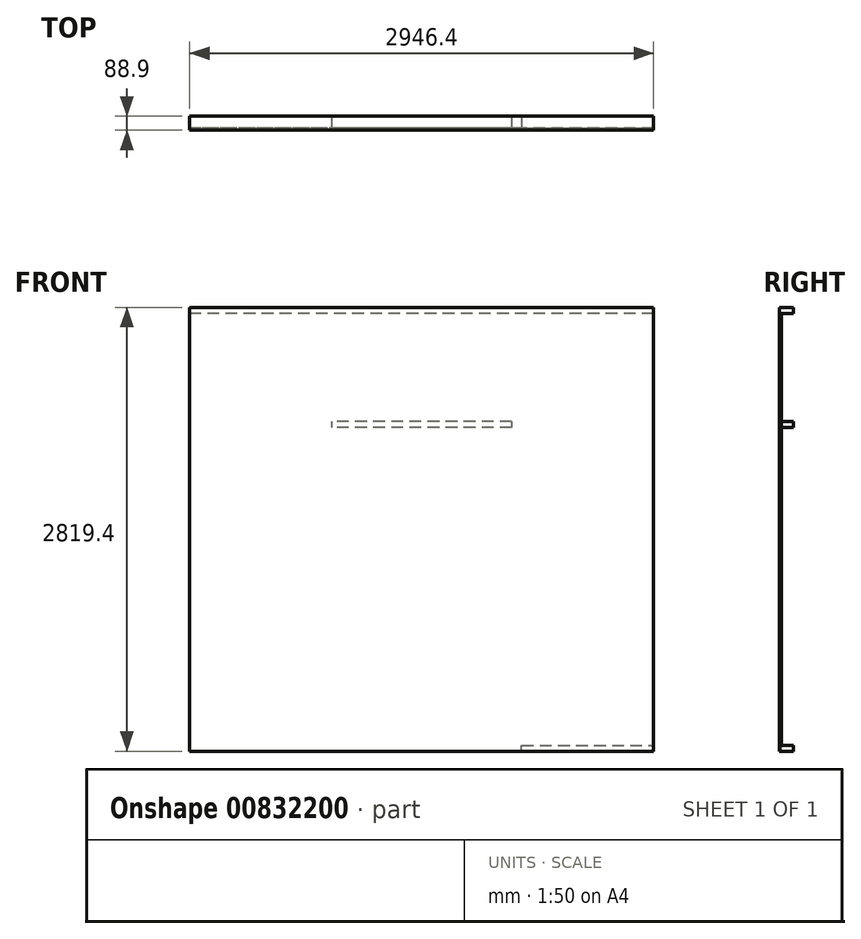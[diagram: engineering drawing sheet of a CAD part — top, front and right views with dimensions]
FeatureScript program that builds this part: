
annotation { "Feature Type Name" : "Feature", "Feature Type Description" : "" }
export const myFeature = defineFeature(function(context is Context, id is Id, definition is map)
    precondition{}
    {
        {
            var Q0;
            Q0=qCreatedBy(makeId("Front.planeOp"),FACE);
            var sketch = newSketch(context, id + "F0", { "sketchPlane" : qUnion([Q0])});
            skLineSegment(sketch, "E0.bottom", {"start": v(1473.2, 1409.7) * mm, "end": v(-1473.2, 1409.7) * mm});
            skLineSegment(sketch, "E0.left", {"start": v(1473.2, 1409.7) * mm, "end": v(1473.2, -1409.7) * mm});
            skLineSegment(sketch, "E0.right", {"start": v(-1473.2, 1409.7) * mm, "end": v(-1473.2, -1409.7) * mm});
            skLineSegment(sketch, "E1.trimOffspring", {"start": v(1473.2, -1409.7) * mm, "end": v(-1473.2, -1409.7) * mm});
            skSolve(sketch);
        }
        {
            var Q0;
            Q0=qSketchRegion(id+"F0",true);
            extrude(context, id + "F1", {"entities" : qUnion([Q0]), "depth" : 12.7 * mm, "offsetDistance" : 25.4 * mm});
        }
        {
            var Q0;
            Q0=makeQuery(id+"F1.opExtrude","CAP_FACE",FACE,{"disambiguationData":[OSD([sQuery(id+"F0.wireOp",EDGE,"E0.bottom"),sQuery(id+"F0.wireOp",EDGE,"E0.top"),sQuery(id+"F0.wireOp",EDGE,"E0.left"),sQuery(id+"F0.wireOp",EDGE,"E0.right"),sQuery(id+"F0.wireOp",EDGE,"iS1P1Vp1-wRpF-BQkS-J5lC-1q9Rx3VtRRPI.top"),sQuery(id+"F0.wireOp",EDGE,"iS1P1Vp1-wRpF-BQkS-J5lC-1q9Rx3VtRRPI.left"),sQuery(id+"F0.wireOp",EDGE,"iS1P1Vp1-wRpF-BQkS-J5lC-1q9Rx3VtRRPI.right"),sQuery(id+"F0.wireOp",EDGE,"E1.trimOffspring")])],"isStart":true});
            var sketch = newSketch(context, id + "F2", { "sketchPlane" : qUnion([Q0])});
            skLineSegment(sketch, "E2.bottom", {"start": v(-1473.2, 1409.7) * mm, "end": v(1473.2, 1409.7) * mm});
            skLineSegment(sketch, "E2.top", {"start": v(-1473.2, 1371.6) * mm, "end": v(1473.2, 1371.6) * mm});
            skLineSegment(sketch, "E2.left", {"start": v(-1473.2, 1409.7) * mm, "end": v(-1473.2, 1371.6) * mm});
            skLineSegment(sketch, "E2.right", {"start": v(1473.2, 1409.7) * mm, "end": v(1473.2, 1371.6) * mm});
            skLineSegment(sketch, "E3.bottom", {"start": v(1473.2, 1371.6) * mm, "end": v(1435.1, 1371.6) * mm});
            skLineSegment(sketch, "E3.top", {"start": v(1473.2, -1371.6) * mm, "end": v(1435.1, -1371.6) * mm});
            skLineSegment(sketch, "E3.left", {"start": v(1473.2, 1371.6) * mm, "end": v(1473.2, -1371.6) * mm});
            skLineSegment(sketch, "E3.right", {"start": v(1435.1, 1371.6) * mm, "end": v(1435.1, -1371.6) * mm});
            skLineSegment(sketch, "E4.bottom", {"start": v(1473.2, -1371.6) * mm, "end": v(-1473.2, -1371.6) * mm});
            skLineSegment(sketch, "E4.top", {"start": v(1473.2, -1409.7) * mm, "end": v(-1473.2, -1409.7) * mm});
            skLineSegment(sketch, "E4.left", {"start": v(1473.2, -1371.6) * mm, "end": v(1473.2, -1409.7) * mm});
            skLineSegment(sketch, "E4.right", {"start": v(-1473.2, -1371.6) * mm, "end": v(-1473.2, -1409.7) * mm});
            skLineSegment(sketch, "E5.bottom", {"start": v(-1473.2, -1371.6) * mm, "end": v(-1435.1, -1371.6) * mm});
            skLineSegment(sketch, "E5.top", {"start": v(-1473.2, 1371.6) * mm, "end": v(-1435.1, 1371.6) * mm});
            skLineSegment(sketch, "E5.left", {"start": v(-1473.2, -1371.6) * mm, "end": v(-1473.2, 1371.6) * mm});
            skLineSegment(sketch, "E5.right", {"start": v(-1435.1, -1371.6) * mm, "end": v(-1435.1, 1371.6) * mm});
            skLineSegment(sketch, "E6.left", {"start": v(-1473.2, 762) * mm, "end": v(-1473.2, 723.9) * mm});
            skLineSegment(sketch, "E7.bottom", {"start": v(-635, -1409.7) * mm, "end": v(-1473.2, -1409.7) * mm});
            skLineSegment(sketch, "E7.top", {"start": v(-635, -1371.6) * mm, "end": v(-1473.2, -1371.6) * mm});
            skLineSegment(sketch, "E7.left", {"start": v(-635, -1409.7) * mm, "end": v(-635, -1371.6) * mm});
            skLineSegment(sketch, "E7.right", {"start": v(-1473.2, -1409.7) * mm, "end": v(-1473.2, -1371.6) * mm});
            skLineSegment(sketch, "E8.bottom", {"start": v(-1079.5, 1371.6) * mm, "end": v(-1041.4, 1371.6) * mm});
            skLineSegment(sketch, "E8.top", {"start": v(-1079.5, -1371.6) * mm, "end": v(-1041.4, -1371.6) * mm});
            skLineSegment(sketch, "E8.left", {"start": v(-1079.5, 1371.6) * mm, "end": v(-1079.5, -1371.6) * mm});
            skLineSegment(sketch, "E8.right", {"start": v(-1041.4, 1371.6) * mm, "end": v(-1041.4, -1371.6) * mm});
            skLineSegment(sketch, "E9.bottom", {"start": v(-635, -1371.6) * mm, "end": v(-673.1, -1371.6) * mm});
            skLineSegment(sketch, "E9.top", {"start": v(-635, 1371.6) * mm, "end": v(-673.1, 1371.6) * mm});
            skLineSegment(sketch, "E10.bottom", {"start": v(1041.4, 1371.6) * mm, "end": v(1079.5, 1371.6) * mm});
            skLineSegment(sketch, "E10.top", {"start": v(1041.4, -1371.6) * mm, "end": v(1079.5, -1371.6) * mm});
            skLineSegment(sketch, "E10.left", {"start": v(1041.4, 1371.6) * mm, "end": v(1041.4, -1371.6) * mm});
            skLineSegment(sketch, "E10.right", {"start": v(1079.5, 1371.6) * mm, "end": v(1079.5, -1371.6) * mm});
            skLineSegment(sketch, "E11.bottom", {"start": v(-1085.85, 1371.6) * mm, "end": v(-1047.75, 1371.6) * mm});
            skLineSegment(sketch, "E12.bottom", {"start": v(-609.6, 1371.6) * mm, "end": v(-571.5, 1371.6) * mm});
            skLineSegment(sketch, "E12.top", {"start": v(-609.6, -1371.6) * mm, "end": v(-571.5, -1371.6) * mm});
            skLineSegment(sketch, "E12.left", {"start": v(-609.6, 1371.6) * mm, "end": v(-609.6, -1371.6) * mm});
            skLineSegment(sketch, "E12.right", {"start": v(-571.5, 1371.6) * mm, "end": v(-571.5, -1371.6) * mm});
            skLineSegment(sketch, "E13.bottom", {"start": v(571.5, 1371.6) * mm, "end": v(609.6, 1371.6) * mm});
            skLineSegment(sketch, "E13.top", {"start": v(571.5, -1371.6) * mm, "end": v(609.6, -1371.6) * mm});
            skLineSegment(sketch, "E13.left", {"start": v(571.5, 1371.6) * mm, "end": v(571.5, -1371.6) * mm});
            skLineSegment(sketch, "E13.right", {"start": v(609.6, 1371.6) * mm, "end": v(609.6, -1371.6) * mm});
            skLineSegment(sketch, "E14.bottom", {"start": v(-571.5, 685.8) * mm, "end": v(571.5, 685.8) * mm});
            skLineSegment(sketch, "E14.top", {"start": v(-571.5, 647.7) * mm, "end": v(571.5, 647.7) * mm});
            skLineSegment(sketch, "E14.left", {"start": v(-571.5, 685.8) * mm, "end": v(-571.5, 647.7) * mm});
            skLineSegment(sketch, "E14.right", {"start": v(571.5, 685.8) * mm, "end": v(571.5, 647.7) * mm});
            skLineSegment(sketch, "E15.bottom", {"start": v(-6.35, 685.8) * mm, "end": v(31.75, 685.8) * mm});
            skLineSegment(sketch, "E15.top", {"start": v(-6.35, 1371.6) * mm, "end": v(31.75, 1371.6) * mm});
            skLineSegment(sketch, "E15.left", {"start": v(-6.35, 685.8) * mm, "end": v(-6.35, 1371.6) * mm});
            skLineSegment(sketch, "E15.right", {"start": v(31.75, 685.8) * mm, "end": v(31.75, 1371.6) * mm});
            skSolve(sketch);
        }
        {
            var Q0;
            {var subQ1=sQuery(id+"F2.wireOp",EDGE,"E8.bottom");Q0=makeQuery(id+"F2.imprint","IMPRINT",FACE,{"disambiguationData":[TD([[makeQuery(id+"F2.imprint","IMPRINT",EDGE,{"derivedFrom":subQ1}),-1.0]])]});}
            var Q1;
            Q1=makeQuery(id+"F2.imprint","IMPRINT",FACE,{"disambiguationData":[TD([[makeQuery(id+"F2.imprint","IMPRINT",EDGE,{"derivedFrom":sQuery(id+"F2.wireOp",EDGE,"E3.bottom")}),1.0]])]});
            var Q2;
            {var subQ0=sQuery(id+"F2.wireOp",EDGE,"E5.bottom");Q2=makeQuery(id+"F2.imprint","IMPRINT",FACE,{"disambiguationData":[TD([[makeQuery(id+"F2.imprint","IMPRINT",EDGE,{"derivedFrom":subQ0}),1.0]])]});}
            var Q3;
            Q3=makeQuery(id+"F2.imprint","IMPRINT",FACE,{"disambiguationData":[TD([[makeQuery(id+"F2.imprint","IMPRINT",EDGE,{"derivedFrom":sQuery(id+"F2.wireOp",EDGE,"E4.top")}),1.0]])]});
            var Q4;
            Q4=makeQuery(id+"F2.imprint","IMPRINT",FACE,{"disambiguationData":[TD([[makeQuery(id+"F2.imprint","IMPRINT",EDGE,{"derivedFrom":sQuery(id+"F2.wireOp",EDGE,"E7.bottom")}),1.0]])]});
            var Q5;
            Q5=makeQuery(id+"F2.imprint","IMPRINT",FACE,{"disambiguationData":[TD([[makeQuery(id+"F2.imprint","IMPRINT",EDGE,{"derivedFrom":sQuery(id+"F2.wireOp",EDGE,"E2.bottom")}),-1.0]])]});
            var Q6;
            Q6=makeQuery(id+"F2.imprint","IMPRINT",FACE,{"disambiguationData":[TD([[makeQuery(id+"F2.imprint","IMPRINT",EDGE,{"derivedFrom":sQuery(id+"F2.wireOp",EDGE,"E10.bottom")}),-1.0]])]});
            var Q7;
            {var subQ1=sQuery(id+"F2.wireOp",EDGE,"E12.bottom");Q7=makeQuery(id+"F2.imprint","IMPRINT",FACE,{"disambiguationData":[TD([[makeQuery(id+"F2.imprint","IMPRINT",EDGE,{"derivedFrom":subQ1}),-1.0]])]});}
            var Q8;
            Q8=makeQuery(id+"F2.imprint","IMPRINT",FACE,{"disambiguationData":[TD([[makeQuery(id+"F2.imprint","IMPRINT",EDGE,{"derivedFrom":sQuery(id+"F2.wireOp",EDGE,"E14.top")}),1.0]])]});
            var Q9;
            Q9=makeQuery(id+"F2.imprint","IMPRINT",FACE,{"disambiguationData":[TD([[makeQuery(id+"F2.imprint","IMPRINT",EDGE,{"derivedFrom":sQuery(id+"F2.wireOp",EDGE,"E15.bottom")}),1.0]])]});
            var Q10;
            {var subQ3=sQuery(id+"F2.wireOp",EDGE,"E13.bottom");Q10=makeQuery(id+"F2.imprint","IMPRINT",FACE,{"disambiguationData":[TD([[makeQuery(id+"F2.imprint","IMPRINT",EDGE,{"derivedFrom":subQ3}),-1.0]])]});}
            extrude(context, id + "F3", {"entities" : qUnion([Q0, Q1, Q2, Q3, Q4, Q5, Q6, Q7, Q8, Q9, Q10]), "operationType" : NewBodyOperationType.ADD, "depth" : 76.2 * mm, "offsetDistance" : 25.4 * mm});
        }
    });
